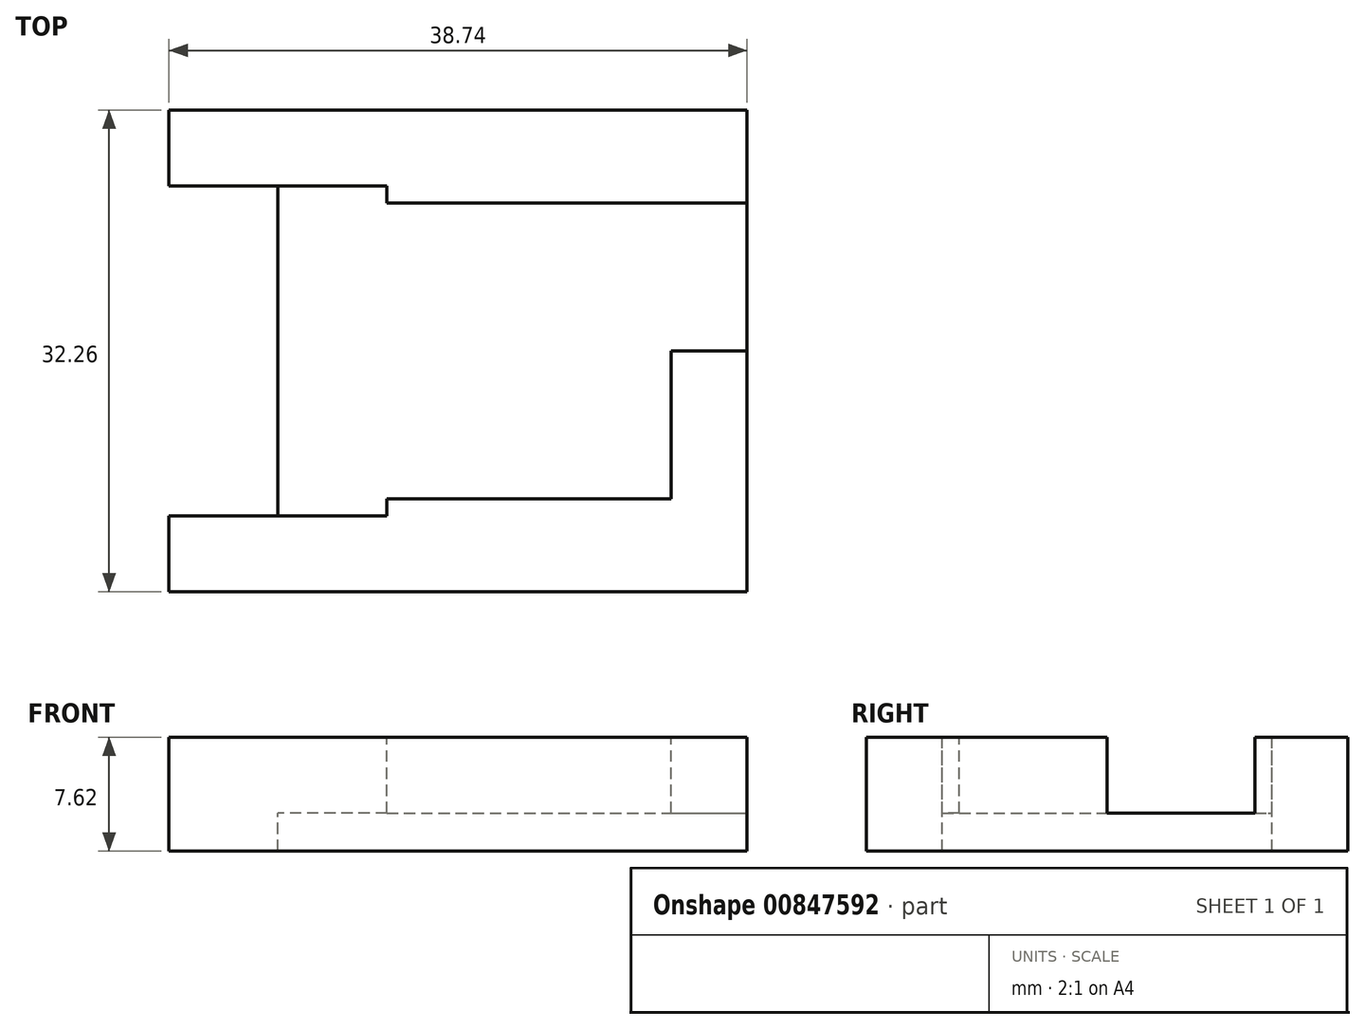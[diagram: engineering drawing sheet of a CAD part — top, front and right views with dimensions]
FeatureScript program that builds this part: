
annotation { "Feature Type Name" : "Feature", "Feature Type Description" : "" }
export const myFeature = defineFeature(function(context is Context, id is Id, definition is map)
    precondition{}
    {
        {
            var Q0;
            Q0=qCreatedBy(makeId("Top.planeOp"),FACE);
            var sketch = newSketch(context, id + "F0", { "sketchPlane" : qUnion([Q0])});
            skLineSegment(sketch, "E0.bottom", {"start": v(0, 0) * mm, "end": v(19.05, 0) * mm});
            skLineSegment(sketch, "E0.top", {"start": v(0, 19.81) * mm, "end": v(19.05, 19.81) * mm});
            skLineSegment(sketch, "E0.left", {"start": v(0, 0) * mm, "end": v(0, 19.81) * mm});
            skLineSegment(sketch, "E0.right", {"start": v(19.05, 0) * mm, "end": v(19.05, 19.81) * mm});
            skLineSegment(sketch, "E1.bottom", {"start": v(0, 0) * mm, "end": v(-14.6, 0) * mm});
            skLineSegment(sketch, "E1.top", {"start": v(0, 20.96) * mm, "end": v(-14.6, 20.95) * mm});
            skLineSegment(sketch, "E1.left", {"start": v(0, 0) * mm, "end": v(0, 20.96) * mm});
            skLineSegment(sketch, "E1.right", {"start": v(-14.6, 0) * mm, "end": v(-14.6, 20.95) * mm});
            skLineSegment(sketch, "E2.top", {"start": v(0, -1.14) * mm, "end": v(-14.6, -1.14) * mm});
            skLineSegment(sketch, "E2.left", {"start": v(0, 0) * mm, "end": v(0, -1.14) * mm});
            skLineSegment(sketch, "E2.right", {"start": v(-14.6, 0) * mm, "end": v(-14.6, -1.14) * mm});
            skSolve(sketch);
        }
        {
            var Q0;
            Q0=makeQuery(id+"F0.imprint","IMPRINT",FACE,{"disambiguationData":[TD([[makeQuery(id+"F0.imprint","IMPRINT",EDGE,{"derivedFrom":sQuery(id+"F0.wireOp",EDGE,"E0.bottom")}),1.0]])]});
            extrude(context, id + "F1", {"entities" : qUnion([Q0]), "depth" : 2.54 * mm, "offsetDistance" : 25.4 * mm});
        }
        {
            var Q0;
            Q0=makeQuery(id+"F0.imprint","IMPRINT",FACE,{"disambiguationData":[TD([[makeQuery(id+"F0.imprint","IMPRINT",EDGE,{"derivedFrom":sQuery(id+"F0.wireOp",EDGE,"E0.left")}),1.0]])]});
            extrude(context, id + "F2", {"entities" : qUnion([Q0]), "operationType" : NewBodyOperationType.ADD, "depth" : 2.54 * mm, "offsetDistance" : 25.4 * mm});
        }
        {
            var Q0;
            Q0=makeQuery(id+"F0.imprint","IMPRINT",FACE,{"disambiguationData":[TD([[makeQuery(id+"F0.imprint","IMPRINT",EDGE,{"derivedFrom":sQuery(id+"F0.wireOp",EDGE,"E1.bottom")}),1.0]])]});
            extrude(context, id + "F3", {"entities" : qUnion([Q0]), "operationType" : NewBodyOperationType.ADD, "depth" : 2.54 * mm, "offsetDistance" : 25.4 * mm});
        }
        {
            var Q0;
            Q0=qCreatedBy(makeId("Top.planeOp"),FACE);
            var sketch = newSketch(context, id + "F4", { "sketchPlane" : qUnion([Q0])});
            skLineSegment(sketch, "E3.bottom", {"start": v(-14.6, 26.04) * mm, "end": v(24.13, 26.04) * mm});
            skLineSegment(sketch, "E3.top", {"start": v(-14.6, -6.22) * mm, "end": v(24.13, -6.22) * mm});
            skLineSegment(sketch, "E3.left", {"start": v(-14.6, 26.04) * mm, "end": v(-14.6, -6.22) * mm});
            skLineSegment(sketch, "E3.right", {"start": v(24.13, 26.04) * mm, "end": v(24.13, -6.22) * mm});
            skSolve(sketch);
        }
        {
            var Q0;
            Q0=makeQuery(id+"F4.imprint","IMPRINT",FACE,{"disambiguationData":[TD([[makeQuery(id+"F4.imprint","IMPRINT",EDGE,{"derivedFrom":sQuery(id+"F4.wireOp",EDGE,"E3.bottom")}),-1.0]])]});
            extrude(context, id + "F5", {"entities" : qUnion([Q0]), "operationType" : NewBodyOperationType.ADD, "oppositeDirection" : true, "depth" : 7.62 * mm, "offsetDistance" : 25.4 * mm});
        }
        {
            var Q0;
            {var subQ0=sQuery(id+"F0.wireOp",EDGE,"E1.bottom");var subQ1=sQuery(id+"F0.wireOp",EDGE,"E0.left");Q0=makeQuery(id+"F3.boolean.opBoolean","MERGE",FACE,{"derivedFrom":[makeQuery(id+"F2.boolean.opBoolean","MERGE",FACE,{"derivedFrom":[makeQuery(id+"F1.opExtrude","CAP_FACE",FACE,{"disambiguationData":[OSD([sQuery(id+"F0.wireOp",EDGE,"E0.bottom"),sQuery(id+"F0.wireOp",EDGE,"E0.top"),subQ1,sQuery(id+"F0.wireOp",EDGE,"E0.right")])],"isStart":false}),makeQuery(id+"F2.opExtrude","CAP_FACE",FACE,{"disambiguationData":[OSD([subQ1,subQ0,sQuery(id+"F0.wireOp",EDGE,"E1.top"),sQuery(id+"F0.wireOp",EDGE,"E1.left"),sQuery(id+"F0.wireOp",EDGE,"E1.right")])],"isStart":false})]}),makeQuery(id+"F3.opExtrude","CAP_FACE",FACE,{"disambiguationData":[OSD([subQ0,sQuery(id+"F0.wireOp",EDGE,"E2.top"),sQuery(id+"F0.wireOp",EDGE,"E2.left"),sQuery(id+"F0.wireOp",EDGE,"E2.right")])],"isStart":false})]});}
            extrude(context, id + "F6", {"entities" : qUnion([Q0]), "operationType" : NewBodyOperationType.REMOVE, "oppositeDirection" : true, "depth" : 7.62 * mm, "offsetDistance" : 25.4 * mm});
        }
        {
            var Q0;
            Q0=makeQuery(id+"F6.boolean.opBoolean","COPY",FACE,{"derivedFrom":makeQuery(id+"F6.opExtrude","CAP_FACE",FACE,{"disambiguationData":[OSD([sQuery(id+"F0.wireOp",EDGE,"E0.bottom"),sQuery(id+"F0.wireOp",EDGE,"E0.top"),sQuery(id+"F0.wireOp",EDGE,"E0.left"),sQuery(id+"F0.wireOp",EDGE,"E0.right"),sQuery(id+"F0.wireOp",EDGE,"E1.bottom"),sQuery(id+"F0.wireOp",EDGE,"E1.top"),sQuery(id+"F0.wireOp",EDGE,"E1.left"),sQuery(id+"F0.wireOp",EDGE,"E1.right"),sQuery(id+"F0.wireOp",EDGE,"E2.top"),sQuery(id+"F0.wireOp",EDGE,"E2.left"),sQuery(id+"F0.wireOp",EDGE,"E2.right")])],"isStart":false})});
            var sketch = newSketch(context, id + "F7", { "sketchPlane" : qUnion([Q0])});
            skLineSegment(sketch, "E4.bottom", {"start": v(-14.6, -1.14) * mm, "end": v(-7.3, -1.14) * mm});
            skLineSegment(sketch, "E4.top", {"start": v(-14.6, 20.95) * mm, "end": v(-7.3, 20.95) * mm});
            skLineSegment(sketch, "E4.left", {"start": v(-14.6, -1.14) * mm, "end": v(-14.6, 20.95) * mm});
            skLineSegment(sketch, "E4.right", {"start": v(-7.3, -1.14) * mm, "end": v(-7.3, 20.95) * mm});
            skSolve(sketch);
        }
        {
            var Q0;
            Q0 = qSketchRegion(id + "F7", true);
            extrude(context, id + "F8", {"entities" : qUnion([Q0]), "operationType" : NewBodyOperationType.REMOVE, "oppositeDirection" : true, "depth" : 2.54 * mm, "offsetDistance" : 25.4 * mm});
        }
        {
            var Q0;
            Q0=makeQuery(id+"F5.opExtrude","CAP_FACE",FACE,{"disambiguationData":[OSD([sQuery(id+"F4.wireOp",EDGE,"E3.bottom"),sQuery(id+"F4.wireOp",EDGE,"E3.top"),sQuery(id+"F4.wireOp",EDGE,"E3.left"),sQuery(id+"F4.wireOp",EDGE,"E3.right")])],"isStart":true});
            var sketch = newSketch(context, id + "F9", { "sketchPlane" : qUnion([Q0])});
            skLineSegment(sketch, "E5.bottom", {"start": v(19.05, 19.81) * mm, "end": v(24.13, 19.81) * mm});
            skLineSegment(sketch, "E5.top", {"start": v(19.05, 9.9) * mm, "end": v(24.13, 9.9) * mm});
            skLineSegment(sketch, "E5.left", {"start": v(19.05, 19.81) * mm, "end": v(19.05, 9.9) * mm});
            skLineSegment(sketch, "E5.right", {"start": v(24.13, 19.81) * mm, "end": v(24.13, 9.9) * mm});
            skSolve(sketch);
        }
        {
            var Q0;
            Q0 = qSketchRegion(id + "F9", true);
            extrude(context, id + "F10", {"entities" : qUnion([Q0]), "operationType" : NewBodyOperationType.REMOVE, "oppositeDirection" : true, "depth" : 5.08 * mm, "offsetDistance" : 25.4 * mm});
        }
    });
